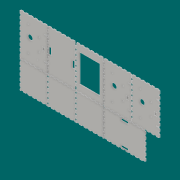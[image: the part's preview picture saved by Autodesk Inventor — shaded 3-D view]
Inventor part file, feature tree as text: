
AUTODESK INVENTOR PART (.ipt)
format: ipt  version: 2016 SP2 (Build 200236200, 236)  size: 1,704,448 bytes
history: native  units: in
note: dims shown in document units (in); Inventor stores cm internally (conversion verified against a paired STEP export)
features: extrude x9, sketch x9, reference x9, plane x8, other x1
ambient origin geometry x8: Origin, YZ Plane, XZ Plane, XY Plane, X Axis, Y Axis, Z Axis, Center Point
bodies: Solid1 (feature_tree)
feature tree (36):
  other  "<userpath>\oneDrive\projects\splitFlapDisplay\parameters.xlsx"
  extrude  "Extrusion1"  Depth=0.0047in
  plane  "Work Plane1"
  extrude  "Extrusion2"  Depth=0.0047in
  plane  "Work Plane2"
  extrude  "Extrusion3"  Depth=0.0047in
  plane  "Work Plane3"
  extrude  "Extrusion4"  Depth=0.0047in
  plane  "Work Plane4"
  extrude  "Extrusion5"  Depth=0.0047in
  plane  "Work Plane5"
  extrude  "Extrusion6"  Depth=0.0047in
  plane  "Work Plane6"
  extrude  "Extrusion7"  Depth=0.125in
  plane  "Work Plane7"
  extrude  "Extrusion8"  Depth=0.0047in
  plane  "Work Plane8"
  extrude  "Extrusion9"  Depth=0.0047in
  sketch  "Sketch1"  dims[d0=0.0047in d1=0.0047in]
  reference  "Reference1"
  sketch  "Sketch2"  dims[d2=0.0047in d3=0.0047in]
  reference  "Reference2"
  sketch  "Sketch3"  dims[d4=0.0047in d5=0.0047in]
  reference  "Reference3"
  sketch  "Sketch4"  dims[d6=0.0047in d7=0.0047in]
  reference  "Reference4"
  sketch  "Sketch5"  dims[d8=0.0047in d9=0.0047in]
  reference  "Reference5"
  sketch  "Sketch6"  dims[d10=0.0047in d11=0.0047in]
  reference  "Reference6"
  sketch  "Sketch7"  dims[d12=0.0047in d13=0.125in]
  reference  "Reference7"
  sketch  "Sketch8"  dims[d14=0.0in d15=0.0047in]
  reference  "Reference8"
  sketch  "Sketch9"  dims[d16=0.0047in d17=0.0047in d18=0.0047in d19=0.0047in d20=0.0047in d21=0.0047in d22=0.125in d23=0.0in d24=0.0047in d25=0.0047in d26=0.125in d27=0.0in d28=0.0047in d29=0.0047in d30=0.0047in d31=0.0047in d32=0.0047in d33=0.0047in d34=0.0047in d35=0.0047in d36=0.0047in d37=0.0047in d38=0.0047in d39=0.125in d40=0.0in d41=0.0047in d42=0.125in d43=0.0in d44=0.0047in d45=0.125in d46=0.0in d47=0.0047in d48=0.125in d49=0.0in d50=0.0047in d51=0.0047in d52=0.0047in d53=0.0047in d54=0.0047in d55=0.0047in d56=0.0047in d57=0.125in d58=0.0in d59=0.0047in d60=0.0047in d61=0.0047in d62=0.0047in d63=0.0047in d64=0.0047in d65=0.0047in d66=0.0047in d67=0.0047in d68=0.0047in d69=0.0047in d70=0.125in d71=0.0in]
  reference  "Reference9"
